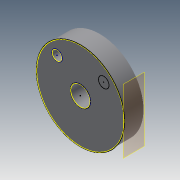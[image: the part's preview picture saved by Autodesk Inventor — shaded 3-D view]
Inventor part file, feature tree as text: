
AUTODESK INVENTOR PART (.ipt)
format: ipt  version: 2015 (Build 190159000, 159)  size: 99,328 bytes
history: native  units: mm
features: other x5, sketch x3, plane x1, extrude x1, projected_geometry x1
ambient origin geometry x8: Origin, YZ Plane, XZ Plane, XY Plane, X Axis, Y Axis, Z Axis, Center Point
bodies: Body1 (feature_tree)
feature tree (11):
  other  "Blocks"
  sketch  "Sketch1"  dims[d0=45.0mm d1=10.0mm]
  plane  "Work Plane1"
  extrude  "Extrusion4"  Depth=10.0mm
  sketch  "Sketch6"  dims[d4=22.5mm]
  sketch  "Sketch7"  dims[d18=5.0mm d19=12.0mm d20=12.0mm d21=10.0mm d22=0.0mm]
  other  "Block1"
  projected_geometry  "Projected Loop3"
  other  "Block2"
  other  "Block2:1"
  other  "Block2:2"
